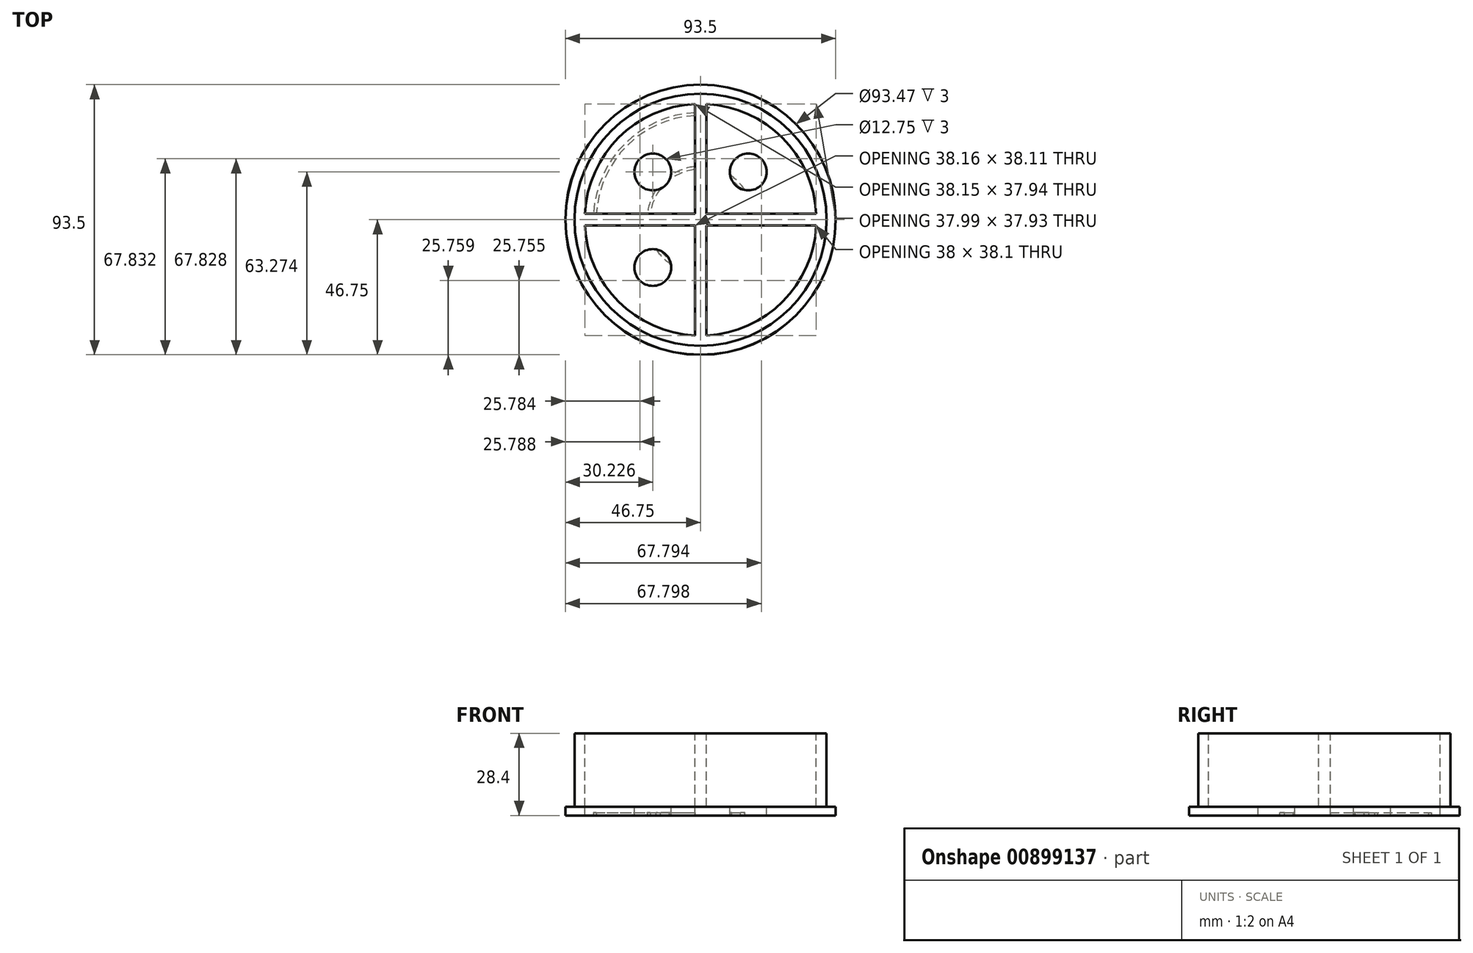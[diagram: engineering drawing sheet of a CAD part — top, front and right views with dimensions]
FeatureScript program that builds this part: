
annotation { "Feature Type Name" : "Feature", "Feature Type Description" : "" }
export const myFeature = defineFeature(function(context is Context, id is Id, definition is map)
    precondition{}
    {
        {
            var Q0;
            Q0=qCreatedBy(makeId("Top.planeOp"),FACE);
            var sketch = newSketch(context, id + "F0", { "sketchPlane" : qUnion([Q0])});
            skCircle(sketch, "E0", {"center": v(0, 0) * mm, "radius": 46.75 * mm});
            skSolve(sketch);
        }
        {
            var Q0;
            Q0=makeQuery(id+"F0.imprint","IMPRINT",FACE,{"disambiguationData":[TD([[makeQuery(id+"F0.imprint","IMPRINT",EDGE,{"derivedFrom":sQuery(id+"F0.wireOp",EDGE,"E0")}),1.0]])]});
            extrude(context, id + "F1", {"entities" : qUnion([Q0]), "depth" : 3 * mm, "offsetDistance" : 25.4 * mm});
        }
        {
            var Q0;
            Q0=makeQuery(id+"F1.opExtrude","CAP_FACE",FACE,{"disambiguationData":[OSD([sQuery(id+"F0.wireOp",EDGE,"E0")])],"isStart":false});
            var sketch = newSketch(context, id + "F2", { "sketchPlane" : qUnion([Q0])});
            skCircle(sketch, "E1", {"center": v(0, 0) * mm, "radius": 43.6 * mm});
            skSolve(sketch);
        }
        {
            var Q0;
            Q0=makeQuery(id+"F2.imprint","IMPRINT",FACE,{"disambiguationData":[TD([[makeQuery(id+"F2.imprint","IMPRINT",EDGE,{"derivedFrom":sQuery(id+"F2.wireOp",EDGE,"E1")}),1.0]])]});
            extrude(context, id + "F3", {"entities" : qUnion([Q0]), "operationType" : NewBodyOperationType.ADD, "depth" : 25.4 * mm, "offsetDistance" : 25.4 * mm});
        }
        {
            var Q0;
            Q0=makeQuery(id+"F1.opExtrude","CAP_FACE",FACE,{"disambiguationData":[OSD([sQuery(id+"F0.wireOp",EDGE,"E0")])],"isStart":true});
            var sketch = newSketch(context, id + "F4", { "sketchPlane" : qUnion([Q0])});
            skCircle(sketch, "E2", {"center": v(0, 0) * mm, "radius": 37.1 * mm});
            skCircle(sketch, "E3.0", {"center": v(0, 0) * mm, "radius": 36.1 * mm});
            skCircle(sketch, "E4", {"center": v(0, 0) * mm, "radius": 18.5 * mm});
            skCircle(sketch, "E5.0", {"center": v(0, 0) * mm, "radius": 17.5 * mm});
            skSolve(sketch);
        }
        {
            var Q0;
            Q0=makeQuery(id+"F4.imprint","IMPRINT",FACE,{"disambiguationData":[TD([[makeQuery(id+"F4.imprint","IMPRINT",EDGE,{"derivedFrom":sQuery(id+"F4.wireOp",EDGE,"E2")}),1.0]])]});
            var Q1;
            Q1=makeQuery(id+"F4.imprint","IMPRINT",FACE,{"disambiguationData":[TD([[makeQuery(id+"F4.imprint","IMPRINT",EDGE,{"derivedFrom":sQuery(id+"F4.wireOp",EDGE,"E4")}),1.0]])]});
            extrude(context, id + "F5", {"entities" : qUnion([Q0, Q1]), "operationType" : NewBodyOperationType.REMOVE, "oppositeDirection" : true, "depth" : 1 * mm, "offsetDistance" : 25.4 * mm});
        }
        {
            var Q0;
            Q0=makeQuery(id+"F3.opExtrude","CAP_FACE",FACE,{"disambiguationData":[OSD([sQuery(id+"F2.wireOp",EDGE,"E1")])],"isStart":false});
            var sketch = newSketch(context, id + "F6", { "sketchPlane" : qUnion([Q0])});
            skLineSegment(sketch, "E6", {"start": v(-1.88, 2.11) * mm, "end": v(-40.04, 2.11) * mm});
            skLineSegment(sketch, "E7", {"start": v(-1.88, 2.11) * mm, "end": v(-1.88, 40.05) * mm});
            skLineSegment(sketch, "E8", {"start": v(2.05, 2.11) * mm, "end": v(40.04, 2.11) * mm});
            skLineSegment(sketch, "E9", {"start": v(2.05, 2.11) * mm, "end": v(2.05, 40.04) * mm});
            skLineSegment(sketch, "E10", {"start": v(2.05, -1.94) * mm, "end": v(40.05, -1.94) * mm});
            skLineSegment(sketch, "E11", {"start": v(-1.88, -1.94) * mm, "end": v(-40.05, -1.94) * mm});
            skLineSegment(sketch, "E12", {"start": v(-1.88, -1.94) * mm, "end": v(-1.88, -40.05) * mm});
            skLineSegment(sketch, "E13", {"start": v(2.05, -1.94) * mm, "end": v(2.05, -40.04) * mm});
            skArc(sketch, "E14", {"start": v(-40.05, -1.94) * mm, "mid": v(-28.33, -28.37) * mm, "end": v(-1.88, -40.05) * mm});
            skArc(sketch, "E15.trimOffspring", {"start": v(2.05, -40.04) * mm, "mid": v(28.39, -28.31) * mm, "end": v(40.05, -1.94) * mm});
            skArc(sketch, "E16.trimOffspring", {"start": v(-1.88, 40.05) * mm, "mid": v(-28.27, 28.43) * mm, "end": v(-40.04, 2.11) * mm});
            skArc(sketch, "E17.trimOffspring", {"start": v(40.04, 2.11) * mm, "mid": v(28.33, 28.37) * mm, "end": v(2.05, 40.04) * mm});
            skSolve(sketch);
        }
        {
            var Q0;
            Q0=makeQuery(id+"F6.imprint","IMPRINT",FACE,{"disambiguationData":[TD([[makeQuery(id+"F6.imprint","IMPRINT",EDGE,{"derivedFrom":sQuery(id+"F6.wireOp",EDGE,"E11")}),1.0]])]});
            var Q1;
            Q1=makeQuery(id+"F6.imprint","IMPRINT",FACE,{"disambiguationData":[TD([[makeQuery(id+"F6.imprint","IMPRINT",EDGE,{"derivedFrom":sQuery(id+"F6.wireOp",EDGE,"E6")}),-1.0]])]});
            var Q2;
            Q2=makeQuery(id+"F6.imprint","IMPRINT",FACE,{"disambiguationData":[TD([[makeQuery(id+"F6.imprint","IMPRINT",EDGE,{"derivedFrom":sQuery(id+"F6.wireOp",EDGE,"E8")}),1.0]])]});
            var Q3;
            Q3=makeQuery(id+"F6.imprint","IMPRINT",FACE,{"disambiguationData":[TD([[makeQuery(id+"F6.imprint","IMPRINT",EDGE,{"derivedFrom":sQuery(id+"F6.wireOp",EDGE,"E10")}),-1.0]])]});
            var Q4;
            Q4=makeQuery(id+"F1.opExtrude","CAP_FACE",FACE,{"disambiguationData":[OSD([sQuery(id+"F0.wireOp",EDGE,"E0")])],"isStart":false});
            extrude(context, id + "F7", {"entities" : qUnion([Q0, Q1, Q2, Q3]), "operationType" : NewBodyOperationType.REMOVE, "endBound" : BoundingType.UP_TO_SURFACE, "oppositeDirection" : true, "depth" : 25.4 * mm, "endBoundEntityFace" : qUnion([Q4]), "offsetDistance" : 25.4 * mm});
        }
        {
            var Q0;
            Q0=makeQuery(id+"F7.boolean.opBoolean","COPY",FACE,{"derivedFrom":makeQuery(id+"F7.opExtrude","CAP_FACE",FACE,{"disambiguationData":[OSD([sQuery(id+"F6.wireOp",EDGE,"E6"),sQuery(id+"F6.wireOp",EDGE,"E7"),sQuery(id+"F6.wireOp",EDGE,"E16.trimOffspring")])],"isStart":false})});
            var sketch = newSketch(context, id + "F8", { "sketchPlane" : qUnion([Q0])});
            skCircle(sketch, "E18", {"center": v(0, 0) * mm, "radius": 46.74 * mm});
            skCircle(sketch, "E19", {"center": v(-16.52, 16.52) * mm, "radius": 6.38 * mm});
            skCircle(sketch, "E20.MirrorC", {"center": v(16.52, 16.52) * mm, "radius": 6.38 * mm});
            skCircle(sketch, "E21.MirrorC", {"center": v(-16.52, -16.52) * mm, "radius": 6.38 * mm});
            skCircle(sketch, "E22.MirrorC", {"center": v(16.52, -16.52) * mm, "radius": 6.38 * mm});
            skSolve(sketch);
        }
        {
            var Q0;
            Q0=makeQuery(id+"F8.imprint","IMPRINT",FACE,{"disambiguationData":[TD([[makeQuery(id+"F8.imprint","IMPRINT",EDGE,{"derivedFrom":sQuery(id+"F8.wireOp",EDGE,"E19")}),1.0]])]});
            var Q1;
            Q1=makeQuery(id+"F8.imprint","IMPRINT",FACE,{"disambiguationData":[TD([[makeQuery(id+"F8.imprint","IMPRINT",EDGE,{"derivedFrom":sQuery(id+"F8.wireOp",EDGE,"E20.MirrorC")}),-1.0]])]});
            var Q2;
            Q2=makeQuery(id+"F8.imprint","IMPRINT",FACE,{"disambiguationData":[TD([[makeQuery(id+"F8.imprint","IMPRINT",EDGE,{"derivedFrom":sQuery(id+"F8.wireOp",EDGE,"E22.MirrorC")}),1.0]])]});
            var Q3;
            Q3=makeQuery(id+"F8.imprint","IMPRINT",FACE,{"disambiguationData":[TD([[makeQuery(id+"F8.imprint","IMPRINT",EDGE,{"derivedFrom":sQuery(id+"F8.wireOp",EDGE,"E21.MirrorC")}),-1.0]])]});
            extrude(context, id + "F9", {"entities" : qUnion([Q0, Q1, Q2, Q3]), "operationType" : NewBodyOperationType.REMOVE, "endBound" : BoundingType.THROUGH_ALL, "oppositeDirection" : true, "depth" : 25.4 * mm, "offsetDistance" : 25.4 * mm});
        }
    });
